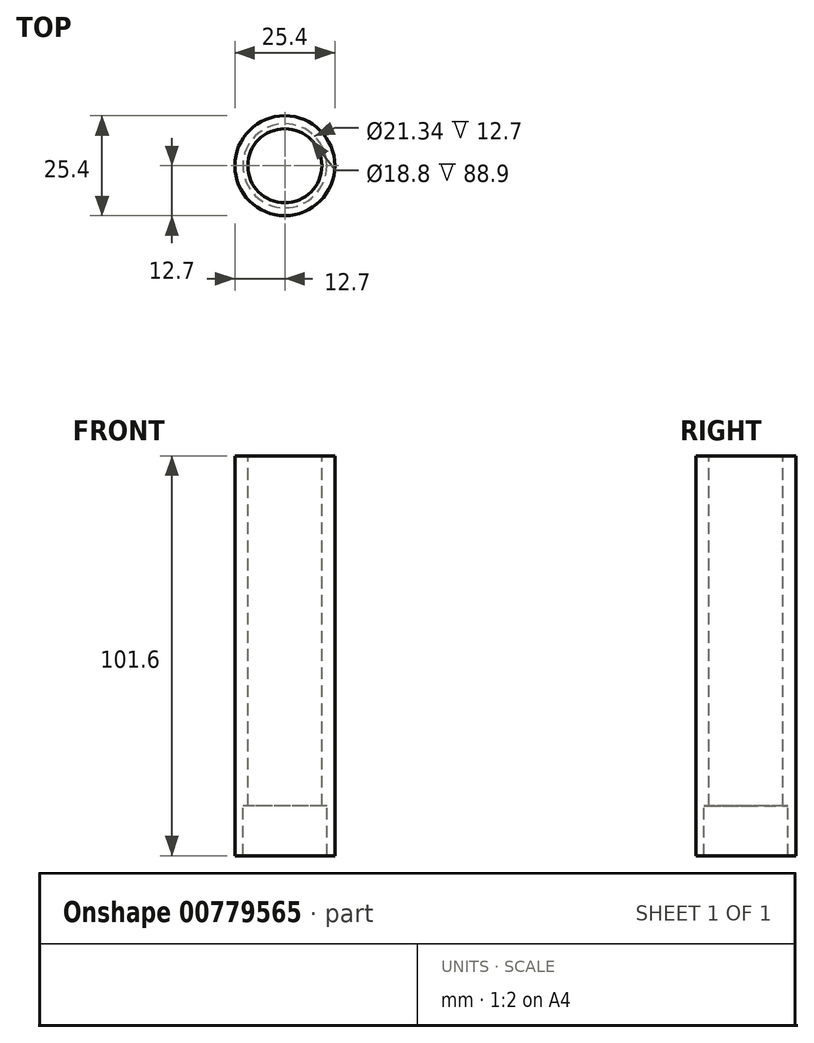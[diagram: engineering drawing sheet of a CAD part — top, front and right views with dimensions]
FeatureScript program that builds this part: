
annotation { "Feature Type Name" : "Feature", "Feature Type Description" : "" }
export const myFeature = defineFeature(function(context is Context, id is Id, definition is map)
    precondition{}
    {
        {
            var Q0;
            Q0=qCreatedBy(makeId("Top.planeOp"),FACE);
            var sketch = newSketch(context, id + "F0", { "sketchPlane" : qUnion([Q0])});
            skCircle(sketch, "E0", {"center": v(0, 0) * mm, "radius": 12.7 * mm});
            skCircle(sketch, "E1.0", {"center": v(0, 0) * mm, "radius": 9.4 * mm});
            skCircle(sketch, "E2.0", {"center": v(0, 0) * mm, "radius": 10.67 * mm});
            skSolve(sketch);
        }
        {
            var Q0;
            Q0 = qSketchRegion(id + "F0", true);
            extrude(context, id + "F1", {"entities" : qUnion([Q0]), "oppositeDirection" : true, "depth" : 101.6 * mm, "offsetDistance" : 25.4 * mm});
        }
        {
            var Q0;
            Q0=makeQuery(id+"F0.imprint","IMPRINT",FACE,{"disambiguationData":[TD([[makeQuery(id+"F0.imprint","IMPRINT",EDGE,{"derivedFrom":sQuery(id+"F0.wireOp",EDGE,"E1.0")}),-1.0]])]});
            extrude(context, id + "F2", {"entities" : qUnion([Q0]), "operationType" : NewBodyOperationType.ADD, "oppositeDirection" : true, "depth" : 88.9 * mm, "offsetDistance" : 25.4 * mm});
        }
    });
